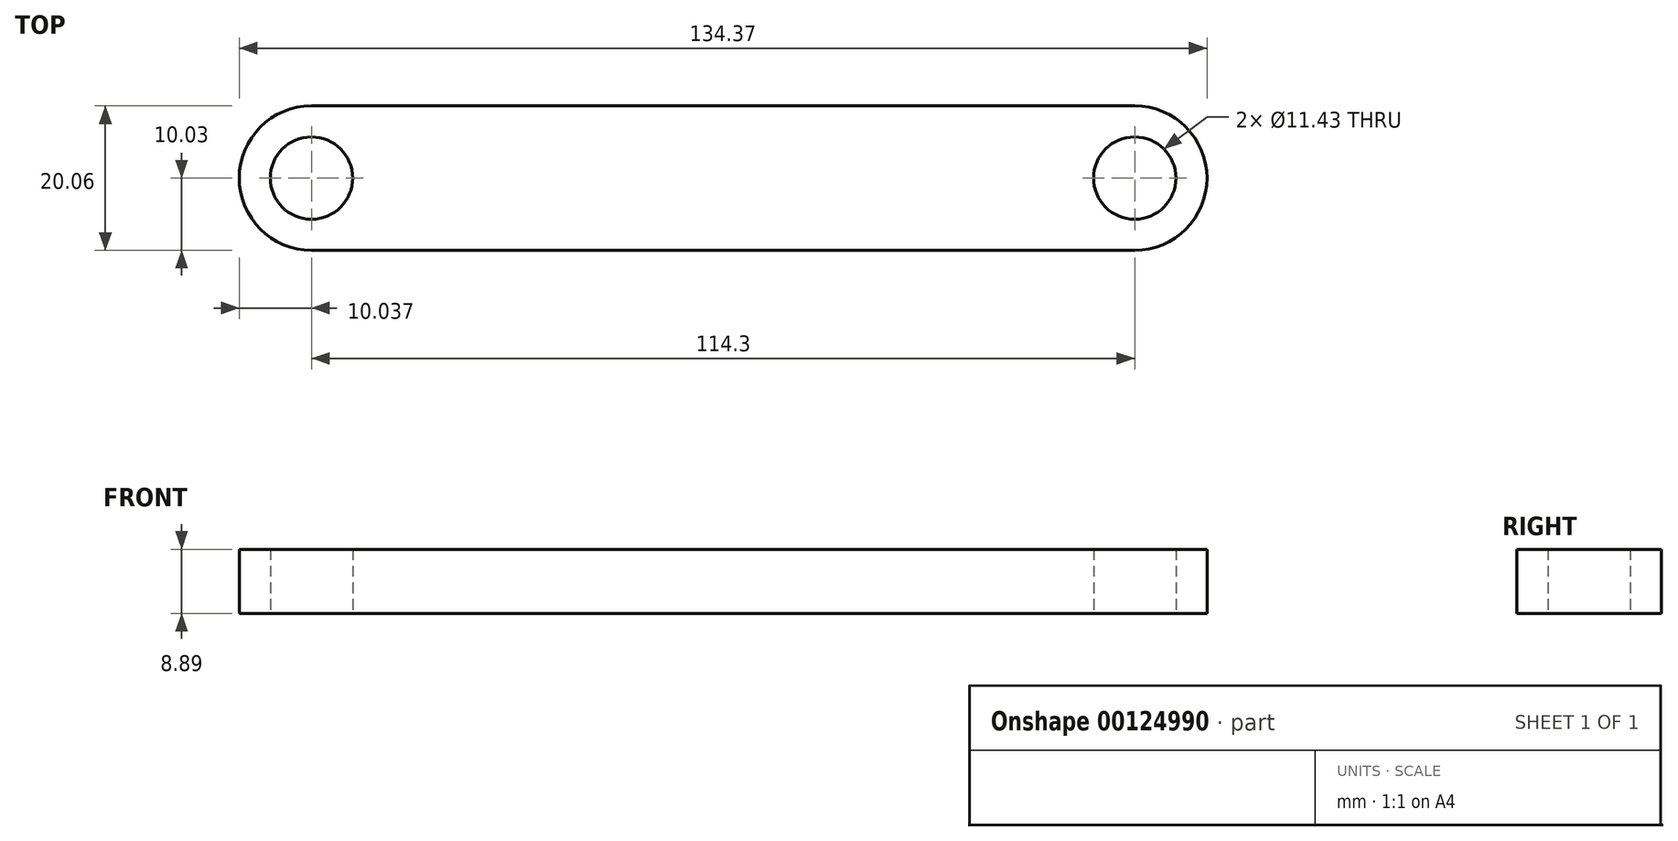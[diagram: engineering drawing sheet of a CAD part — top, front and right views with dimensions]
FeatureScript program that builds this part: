
annotation { "Feature Type Name" : "Feature", "Feature Type Description" : "" }
export const myFeature = defineFeature(function(context is Context, id is Id, definition is map)
    precondition{}
    {
        {
            var Q0;
            Q0=qCreatedBy(makeId("Top.planeOp"),FACE);
            var sketch = newSketch(context, id + "F0", { "sketchPlane" : qUnion([Q0])});
            skCircle(sketch, "E0", {"center": v(-87.98, 0) * mm, "radius": 10.03 * mm});
            skCircle(sketch, "E1", {"center": v(26.32, 0) * mm, "radius": 10.03 * mm});
            skLineSegment(sketch, "E2", {"start": v(-87.98, -10.03) * mm, "end": v(26.32, -10.03) * mm});
            skLineSegment(sketch, "E3", {"start": v(-87.98, 10.03) * mm, "end": v(26.32, 10.03) * mm});
            skCircle(sketch, "E4", {"center": v(26.32, 0) * mm, "radius": 5.72 * mm});
            skCircle(sketch, "E5", {"center": v(-87.98, 0) * mm, "radius": 5.72 * mm});
            skSolve(sketch);
        }
        {
            var Q0;
            {var subQ0=sQuery(id+"F0.wireOp",EDGE,"E2");Q0=makeQuery(id+"F0.imprint","IMPRINT",FACE,{"disambiguationData":[TD([[makeQuery(id+"F0.imprint","IMPRINT",EDGE,{"derivedFrom":subQ0}),1.0]])]});}
            var Q1;
            Q1=makeQuery(id+"F0.imprint","IMPRINT",FACE,{"disambiguationData":[TD([[makeQuery(id+"F0.imprint","IMPRINT",EDGE,{"derivedFrom":sQuery(id+"F0.wireOp",EDGE,"E5")}),-1.0]])]});
            var Q2;
            Q2=makeQuery(id+"F0.imprint","IMPRINT",FACE,{"disambiguationData":[TD([[makeQuery(id+"F0.imprint","IMPRINT",EDGE,{"derivedFrom":sQuery(id+"F0.wireOp",EDGE,"E4")}),-1.0]])]});
            extrude(context, id + "F1", {"entities" : qUnion([Q0, Q1, Q2]), "depth" : 8.9 * mm});
        }
        {
            var Q0;
            Q0=sQuery(id+"F0.wireOp",EDGE,"E4");
            extrude(context, id + "F2", {"bodyType" : ToolBodyType.SURFACE, "surfaceEntities" : qUnion([Q0]), "depth" : 25.4 * mm});
        }
        {
            var Q0;
            Q0=sQuery(id+"F0.wireOp",EDGE,"E5");
            extrude(context, id + "F3", {"bodyType" : ToolBodyType.SURFACE, "surfaceEntities" : qUnion([Q0]), "depth" : 14.75 * mm});
        }
    });
